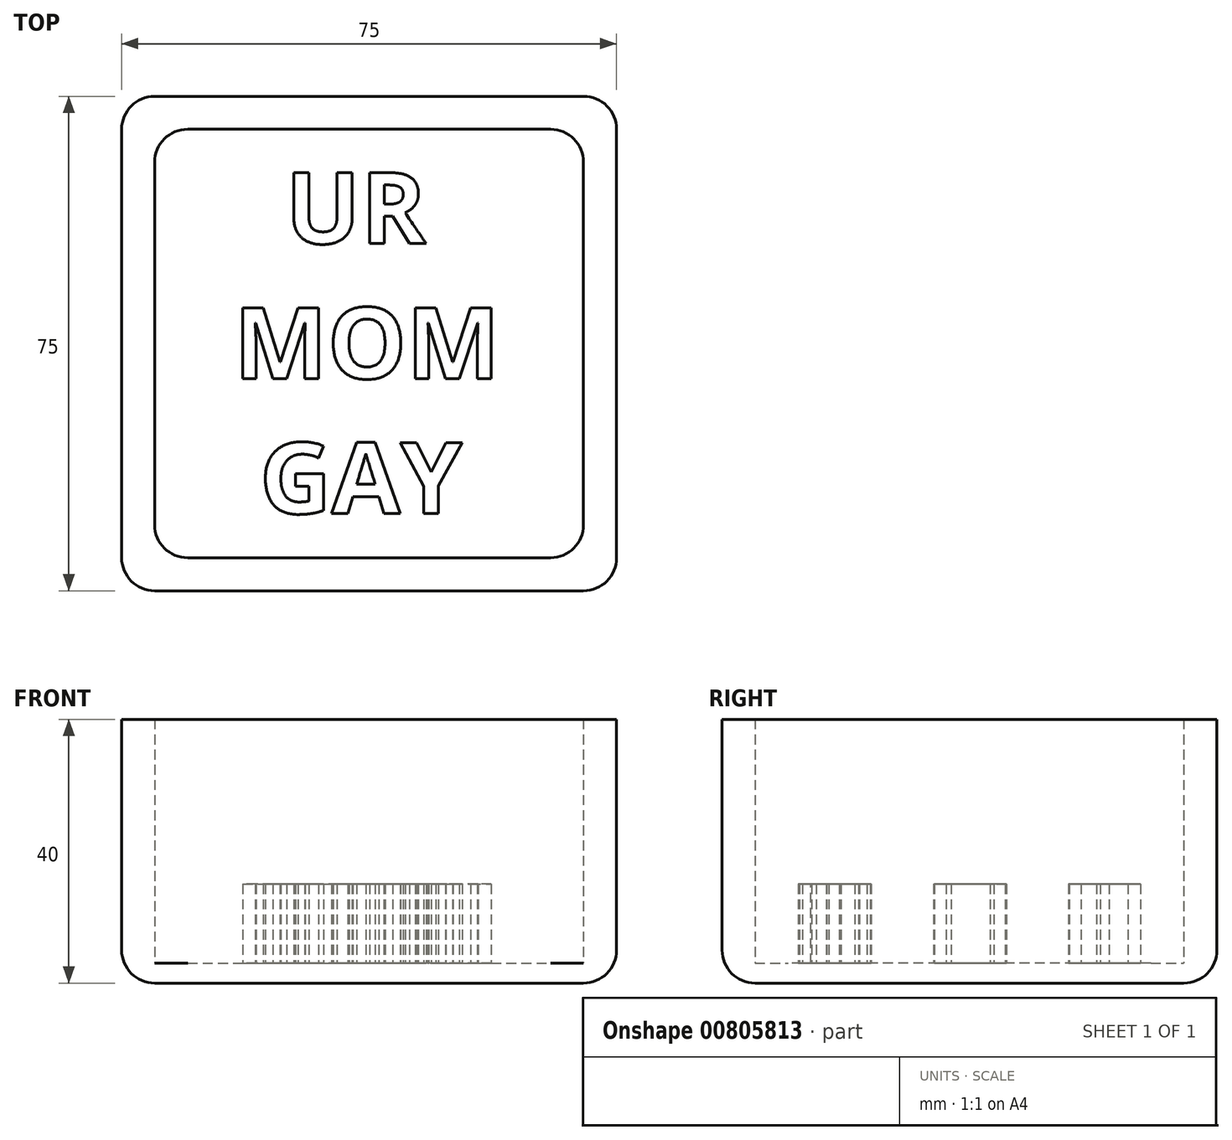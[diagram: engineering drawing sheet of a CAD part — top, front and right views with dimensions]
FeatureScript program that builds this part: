
annotation { "Feature Type Name" : "Feature", "Feature Type Description" : "" }
export const myFeature = defineFeature(function(context is Context, id is Id, definition is map)
    precondition{}
    {
        {
            var Q0;
            Q0=qCreatedBy(makeId("Top.planeOp"),FACE);
            var sketch = newSketch(context, id + "F0", { "sketchPlane" : qUnion([Q0])});
            skLineSegment(sketch, "E0.bottom", {"start": v(-33.51, 30.16) * mm, "end": v(41.49, 30.16) * mm});
            skLineSegment(sketch, "E0.top", {"start": v(-33.51, -44.84) * mm, "end": v(41.49, -44.84) * mm});
            skLineSegment(sketch, "E0.left", {"start": v(-33.51, 30.16) * mm, "end": v(-33.51, -44.84) * mm});
            skLineSegment(sketch, "E0.right", {"start": v(41.49, 30.16) * mm, "end": v(41.49, -44.84) * mm});
            skLineSegment(sketch, "E1.bottom", {"start": v(-28.51, 25.16) * mm, "end": v(36.49, 25.16) * mm});
            skLineSegment(sketch, "E1.top", {"start": v(-28.51, -39.84) * mm, "end": v(36.49, -39.84) * mm});
            skLineSegment(sketch, "E1.left", {"start": v(-28.51, 25.16) * mm, "end": v(-28.51, -39.84) * mm});
            skLineSegment(sketch, "E1.right", {"start": v(36.49, 25.16) * mm, "end": v(36.49, -39.84) * mm});
            skSolve(sketch);
        }
        {
            var Q0;
            Q0 = qSketchRegion(id + "F0", true);
            extrude(context, id + "F1", {"entities" : qUnion([Q0]), "depth" : 15 * mm, "offsetDistance" : 25 * mm});
        }
        {
            var Q0;
            Q0=makeQuery(id+"F0.imprint","IMPRINT",FACE,{"disambiguationData":[TD([[makeQuery(id+"F0.imprint","IMPRINT",EDGE,{"derivedFrom":sQuery(id+"F0.wireOp",EDGE,"E1.bottom")}),-1.0]])]});
            extrude(context, id + "F2", {"entities" : qUnion([Q0]), "operationType" : NewBodyOperationType.ADD, "depth" : 3 * mm, "offsetDistance" : 25 * mm});
        }
        {
            var Q0;
            Q0=makeQuery(id+"F1.opExtrude","SWEPT_EDGE",EDGE,{"disambiguationData":[OSD([sQuery(id+"F0.wireOp",EDGE,"E0.top"),sQuery(id+"F0.wireOp",EDGE,"E0.left")])]});
            var Q1;
            Q1=makeQuery(id+"F1.opExtrude","SWEPT_EDGE",EDGE,{"disambiguationData":[OSD([sQuery(id+"F0.wireOp",EDGE,"E0.top"),sQuery(id+"F0.wireOp",EDGE,"E0.right")])]});
            var Q2;
            Q2=makeQuery(id+"F1.opExtrude","SWEPT_EDGE",EDGE,{"disambiguationData":[OSD([sQuery(id+"F0.wireOp",EDGE,"E0.bottom"),sQuery(id+"F0.wireOp",EDGE,"E0.right")])]});
            var Q3;
            Q3=makeQuery(id+"F1.opExtrude","SWEPT_EDGE",EDGE,{"disambiguationData":[OSD([sQuery(id+"F0.wireOp",EDGE,"E0.bottom"),sQuery(id+"F0.wireOp",EDGE,"E0.left")])]});
            var Q4;
            Q4=makeQuery(id+"F1.opExtrude","CAP_EDGE",EDGE,{"disambiguationData":[OSD([sQuery(id+"F0.wireOp",EDGE,"E0.bottom")])],"isStart":true});
            var Q5;
            Q5=makeQuery(id+"F1.opExtrude","CAP_EDGE",EDGE,{"disambiguationData":[OSD([sQuery(id+"F0.wireOp",EDGE,"E0.right")])],"isStart":true});
            var Q6;
            Q6=makeQuery(id+"F1.opExtrude","CAP_EDGE",EDGE,{"disambiguationData":[OSD([sQuery(id+"F0.wireOp",EDGE,"E0.top")])],"isStart":true});
            var Q7;
            Q7=makeQuery(id+"F1.opExtrude","CAP_EDGE",EDGE,{"disambiguationData":[OSD([sQuery(id+"F0.wireOp",EDGE,"E0.left")])],"isStart":true});
            var Q8;
            Q8=makeQuery(id+"F2.opExtrude","CAP_EDGE",EDGE,{"disambiguationData":[OSD([sQuery(id+"F0.wireOp",EDGE,"E1.bottom")])],"isStart":false});
            var Q9;
            Q9=makeQuery(id+"F2.opExtrude","CAP_EDGE",EDGE,{"disambiguationData":[OSD([sQuery(id+"F0.wireOp",EDGE,"E1.right")])],"isStart":false});
            var Q10;
            Q10=makeQuery(id+"F2.opExtrude","CAP_EDGE",EDGE,{"disambiguationData":[OSD([sQuery(id+"F0.wireOp",EDGE,"E1.left")])],"isStart":false});
            var Q11;
            Q11=makeQuery(id+"F2.opExtrude","CAP_EDGE",EDGE,{"disambiguationData":[OSD([sQuery(id+"F0.wireOp",EDGE,"E1.top")])],"isStart":false});
            fillet(context, id + "F3", {"entities" : qUnion([Q0, Q1, Q2, Q3, Q4, Q5, Q6, Q7, Q8, Q9, Q10, Q11]), "radius" : 5 * mm, "tangentPropagation" : true, "allowEdgeOverflow" : false});
        }
        {
            var Q0;
            Q0=makeQuery(id+"F2.opExtrude","CAP_FACE",FACE,{"disambiguationData":[OSD([sQuery(id+"F0.wireOp",EDGE,"E1.bottom"),sQuery(id+"F0.wireOp",EDGE,"E1.top"),sQuery(id+"F0.wireOp",EDGE,"E1.left"),sQuery(id+"F0.wireOp",EDGE,"E1.right")])],"isStart":false});
            var sketch = newSketch(context, id + "F4", { "sketchPlane" : qUnion([Q0])});
            skText(sketch, "E2", { "text": "  UR\nMOM\n GAY", "fontName": "OpenSans-Bold.ttf"});
            const initialGuessF4  = {"E2": [-0.01651, 0.00782, 1, 0, 0.01084]};
            skSetInitialGuess(sketch, initialGuessF4);
            skSolve(sketch);
        }
        {
            var Q0;
            Q0 = qSketchRegion(id + "F4", true);
            extrude(context, id + "F5", {"entities" : qUnion([Q0]), "operationType" : NewBodyOperationType.ADD, "depth" : 5 * mm, "offsetDistance" : 25 * mm});
        }
        {
            var Q0;
            Q0=makeQuery(id+"F1.opExtrude","SWEPT_EDGE",EDGE,{"disambiguationData":[OSD([sQuery(id+"F0.wireOp",EDGE,"E1.bottom"),sQuery(id+"F0.wireOp",EDGE,"E1.left")])]});
            var Q1;
            Q1=makeQuery(id+"F1.opExtrude","SWEPT_EDGE",EDGE,{"disambiguationData":[OSD([sQuery(id+"F0.wireOp",EDGE,"E1.bottom"),sQuery(id+"F0.wireOp",EDGE,"E1.right")])]});
            var Q2;
            Q2=makeQuery(id+"F1.opExtrude","SWEPT_EDGE",EDGE,{"disambiguationData":[OSD([sQuery(id+"F0.wireOp",EDGE,"E1.top"),sQuery(id+"F0.wireOp",EDGE,"E1.left")])]});
            var Q3;
            Q3=makeQuery(id+"F1.opExtrude","SWEPT_EDGE",EDGE,{"disambiguationData":[OSD([sQuery(id+"F0.wireOp",EDGE,"E1.top"),sQuery(id+"F0.wireOp",EDGE,"E1.right")])]});
            fillet(context, id + "F6", {"entities" : qUnion([Q0, Q1, Q2, Q3]), "radius" : 5 * mm, "tangentPropagation" : true, "allowEdgeOverflow" : false});
        }
        {
            var Q0;
            Q0=makeQuery(id+"F5.opExtrude","CAP_FACE",FACE,{"disambiguationData":[OSD([sQuery(id+"F4.wireOp",EDGE,"E2.sketch_text.stroke-34"),sQuery(id+"F4.wireOp",EDGE,"E2.sketch_text.stroke-35"),sQuery(id+"F4.wireOp",EDGE,"E2.sketch_text.stroke-36"),sQuery(id+"F4.wireOp",EDGE,"E2.sketch_text.stroke-37"),sQuery(id+"F4.wireOp",EDGE,"E2.sketch_text.stroke-38"),sQuery(id+"F4.wireOp",EDGE,"E2.sketch_text.stroke-39"),sQuery(id+"F4.wireOp",EDGE,"E2.sketch_text.stroke-40"),sQuery(id+"F4.wireOp",EDGE,"E2.sketch_text.stroke-41"),sQuery(id+"F4.wireOp",EDGE,"E2.sketch_text.stroke-42"),sQuery(id+"F4.wireOp",EDGE,"E2.sketch_text.stroke-43"),sQuery(id+"F4.wireOp",EDGE,"E2.sketch_text.stroke-44"),sQuery(id+"F4.wireOp",EDGE,"E2.sketch_text.stroke-45"),sQuery(id+"F4.wireOp",EDGE,"E2.sketch_text.stroke-46"),sQuery(id+"F4.wireOp",EDGE,"E2.sketch_text.stroke-47"),sQuery(id+"F4.wireOp",EDGE,"E2.sketch_text.stroke-48"),sQuery(id+"F4.wireOp",EDGE,"E2.sketch_text.stroke-49"),sQuery(id+"F4.wireOp",EDGE,"E2.sketch_text.stroke-50"),sQuery(id+"F4.wireOp",EDGE,"E2.sketch_text.stroke-51"),sQuery(id+"F4.wireOp",EDGE,"E2.sketch_text.stroke-52")])],"isStart":false});
            var Q1;
            Q1=makeQuery(id+"F5.opExtrude","CAP_FACE",FACE,{"disambiguationData":[OSD([sQuery(id+"F4.wireOp",EDGE,"E2.sketch_text.stroke-53"),sQuery(id+"F4.wireOp",EDGE,"E2.sketch_text.stroke-54"),sQuery(id+"F4.wireOp",EDGE,"E2.sketch_text.stroke-55"),sQuery(id+"F4.wireOp",EDGE,"E2.sketch_text.stroke-56"),sQuery(id+"F4.wireOp",EDGE,"E2.sketch_text.stroke-57"),sQuery(id+"F4.wireOp",EDGE,"E2.sketch_text.stroke-58"),sQuery(id+"F4.wireOp",EDGE,"E2.sketch_text.stroke-59"),sQuery(id+"F4.wireOp",EDGE,"E2.sketch_text.stroke-60"),sQuery(id+"F4.wireOp",EDGE,"E2.sketch_text.stroke-61"),sQuery(id+"F4.wireOp",EDGE,"E2.sketch_text.stroke-62"),sQuery(id+"F4.wireOp",EDGE,"E2.sketch_text.stroke-63"),sQuery(id+"F4.wireOp",EDGE,"E2.sketch_text.stroke-64"),sQuery(id+"F4.wireOp",EDGE,"E2.sketch_text.stroke-65"),sQuery(id+"F4.wireOp",EDGE,"E2.sketch_text.stroke-66")])],"isStart":false});
            var Q2;
            Q2=makeQuery(id+"F5.opExtrude","CAP_FACE",FACE,{"disambiguationData":[OSD([sQuery(id+"F4.wireOp",EDGE,"E2.sketch_text.stroke-67"),sQuery(id+"F4.wireOp",EDGE,"E2.sketch_text.stroke-68"),sQuery(id+"F4.wireOp",EDGE,"E2.sketch_text.stroke-69"),sQuery(id+"F4.wireOp",EDGE,"E2.sketch_text.stroke-70"),sQuery(id+"F4.wireOp",EDGE,"E2.sketch_text.stroke-71"),sQuery(id+"F4.wireOp",EDGE,"E2.sketch_text.stroke-72"),sQuery(id+"F4.wireOp",EDGE,"E2.sketch_text.stroke-73"),sQuery(id+"F4.wireOp",EDGE,"E2.sketch_text.stroke-74"),sQuery(id+"F4.wireOp",EDGE,"E2.sketch_text.stroke-75"),sQuery(id+"F4.wireOp",EDGE,"E2.sketch_text.stroke-76"),sQuery(id+"F4.wireOp",EDGE,"E2.sketch_text.stroke-77"),sQuery(id+"F4.wireOp",EDGE,"E2.sketch_text.stroke-78"),sQuery(id+"F4.wireOp",EDGE,"E2.sketch_text.stroke-79"),sQuery(id+"F4.wireOp",EDGE,"E2.sketch_text.stroke-80"),sQuery(id+"F4.wireOp",EDGE,"E2.sketch_text.stroke-81"),sQuery(id+"F4.wireOp",EDGE,"E2.sketch_text.stroke-82"),sQuery(id+"F4.wireOp",EDGE,"E2.sketch_text.stroke-83"),sQuery(id+"F4.wireOp",EDGE,"E2.sketch_text.stroke-84"),sQuery(id+"F4.wireOp",EDGE,"E2.sketch_text.stroke-85")])],"isStart":false});
            var Q3;
            Q3=makeQuery(id+"F5.opExtrude","CAP_FACE",FACE,{"disambiguationData":[OSD([sQuery(id+"F4.wireOp",EDGE,"E2.sketch_text.stroke-15"),sQuery(id+"F4.wireOp",EDGE,"E2.sketch_text.stroke-16"),sQuery(id+"F4.wireOp",EDGE,"E2.sketch_text.stroke-17"),sQuery(id+"F4.wireOp",EDGE,"E2.sketch_text.stroke-18"),sQuery(id+"F4.wireOp",EDGE,"E2.sketch_text.stroke-19"),sQuery(id+"F4.wireOp",EDGE,"E2.sketch_text.stroke-20"),sQuery(id+"F4.wireOp",EDGE,"E2.sketch_text.stroke-21"),sQuery(id+"F4.wireOp",EDGE,"E2.sketch_text.stroke-22"),sQuery(id+"F4.wireOp",EDGE,"E2.sketch_text.stroke-23"),sQuery(id+"F4.wireOp",EDGE,"E2.sketch_text.stroke-24"),sQuery(id+"F4.wireOp",EDGE,"E2.sketch_text.stroke-25"),sQuery(id+"F4.wireOp",EDGE,"E2.sketch_text.stroke-26"),sQuery(id+"F4.wireOp",EDGE,"E2.sketch_text.stroke-27"),sQuery(id+"F4.wireOp",EDGE,"E2.sketch_text.stroke-28"),sQuery(id+"F4.wireOp",EDGE,"E2.sketch_text.stroke-29"),sQuery(id+"F4.wireOp",EDGE,"E2.sketch_text.stroke-30"),sQuery(id+"F4.wireOp",EDGE,"E2.sketch_text.stroke-31"),sQuery(id+"F4.wireOp",EDGE,"E2.sketch_text.stroke-32"),sQuery(id+"F4.wireOp",EDGE,"E2.sketch_text.stroke-33")])],"isStart":false});
            var Q4;
            Q4=makeQuery(id+"F5.opExtrude","CAP_FACE",FACE,{"disambiguationData":[OSD([sQuery(id+"F4.wireOp",EDGE,"E2.sketch_text.stroke-0"),sQuery(id+"F4.wireOp",EDGE,"E2.sketch_text.stroke-1"),sQuery(id+"F4.wireOp",EDGE,"E2.sketch_text.stroke-2"),sQuery(id+"F4.wireOp",EDGE,"E2.sketch_text.stroke-3"),sQuery(id+"F4.wireOp",EDGE,"E2.sketch_text.stroke-4"),sQuery(id+"F4.wireOp",EDGE,"E2.sketch_text.stroke-5"),sQuery(id+"F4.wireOp",EDGE,"E2.sketch_text.stroke-6"),sQuery(id+"F4.wireOp",EDGE,"E2.sketch_text.stroke-7"),sQuery(id+"F4.wireOp",EDGE,"E2.sketch_text.stroke-8"),sQuery(id+"F4.wireOp",EDGE,"E2.sketch_text.stroke-9"),sQuery(id+"F4.wireOp",EDGE,"E2.sketch_text.stroke-10"),sQuery(id+"F4.wireOp",EDGE,"E2.sketch_text.stroke-11"),sQuery(id+"F4.wireOp",EDGE,"E2.sketch_text.stroke-12"),sQuery(id+"F4.wireOp",EDGE,"E2.sketch_text.stroke-13"),sQuery(id+"F4.wireOp",EDGE,"E2.sketch_text.stroke-14")])],"isStart":false});
            var Q5;
            Q5=makeQuery(id+"F5.opExtrude","CAP_FACE",FACE,{"disambiguationData":[OSD([sQuery(id+"F4.wireOp",EDGE,"E2.sketch_text.stroke-117"),sQuery(id+"F4.wireOp",EDGE,"E2.sketch_text.stroke-118"),sQuery(id+"F4.wireOp",EDGE,"E2.sketch_text.stroke-119"),sQuery(id+"F4.wireOp",EDGE,"E2.sketch_text.stroke-120"),sQuery(id+"F4.wireOp",EDGE,"E2.sketch_text.stroke-121"),sQuery(id+"F4.wireOp",EDGE,"E2.sketch_text.stroke-122"),sQuery(id+"F4.wireOp",EDGE,"E2.sketch_text.stroke-123"),sQuery(id+"F4.wireOp",EDGE,"E2.sketch_text.stroke-124"),sQuery(id+"F4.wireOp",EDGE,"E2.sketch_text.stroke-125")])],"isStart":false});
            var Q6;
            Q6=makeQuery(id+"F5.opExtrude","CAP_FACE",FACE,{"disambiguationData":[OSD([sQuery(id+"F4.wireOp",EDGE,"E2.sketch_text.stroke-105"),sQuery(id+"F4.wireOp",EDGE,"E2.sketch_text.stroke-106"),sQuery(id+"F4.wireOp",EDGE,"E2.sketch_text.stroke-107"),sQuery(id+"F4.wireOp",EDGE,"E2.sketch_text.stroke-108"),sQuery(id+"F4.wireOp",EDGE,"E2.sketch_text.stroke-109"),sQuery(id+"F4.wireOp",EDGE,"E2.sketch_text.stroke-110"),sQuery(id+"F4.wireOp",EDGE,"E2.sketch_text.stroke-111"),sQuery(id+"F4.wireOp",EDGE,"E2.sketch_text.stroke-112"),sQuery(id+"F4.wireOp",EDGE,"E2.sketch_text.stroke-113"),sQuery(id+"F4.wireOp",EDGE,"E2.sketch_text.stroke-114"),sQuery(id+"F4.wireOp",EDGE,"E2.sketch_text.stroke-115"),sQuery(id+"F4.wireOp",EDGE,"E2.sketch_text.stroke-116")])],"isStart":false});
            var Q7;
            Q7=makeQuery(id+"F5.opExtrude","CAP_FACE",FACE,{"disambiguationData":[OSD([sQuery(id+"F4.wireOp",EDGE,"E2.sketch_text.stroke-86"),sQuery(id+"F4.wireOp",EDGE,"E2.sketch_text.stroke-87"),sQuery(id+"F4.wireOp",EDGE,"E2.sketch_text.stroke-88"),sQuery(id+"F4.wireOp",EDGE,"E2.sketch_text.stroke-89"),sQuery(id+"F4.wireOp",EDGE,"E2.sketch_text.stroke-90"),sQuery(id+"F4.wireOp",EDGE,"E2.sketch_text.stroke-91"),sQuery(id+"F4.wireOp",EDGE,"E2.sketch_text.stroke-92"),sQuery(id+"F4.wireOp",EDGE,"E2.sketch_text.stroke-93"),sQuery(id+"F4.wireOp",EDGE,"E2.sketch_text.stroke-94"),sQuery(id+"F4.wireOp",EDGE,"E2.sketch_text.stroke-95"),sQuery(id+"F4.wireOp",EDGE,"E2.sketch_text.stroke-96"),sQuery(id+"F4.wireOp",EDGE,"E2.sketch_text.stroke-97"),sQuery(id+"F4.wireOp",EDGE,"E2.sketch_text.stroke-98"),sQuery(id+"F4.wireOp",EDGE,"E2.sketch_text.stroke-99"),sQuery(id+"F4.wireOp",EDGE,"E2.sketch_text.stroke-100"),sQuery(id+"F4.wireOp",EDGE,"E2.sketch_text.stroke-101"),sQuery(id+"F4.wireOp",EDGE,"E2.sketch_text.stroke-102"),sQuery(id+"F4.wireOp",EDGE,"E2.sketch_text.stroke-103"),sQuery(id+"F4.wireOp",EDGE,"E2.sketch_text.stroke-104")])],"isStart":false});
            extrude(context, id + "F7", {"entities" : qUnion([Q0, Q1, Q2, Q3, Q4, Q5, Q6, Q7]), "operationType" : NewBodyOperationType.ADD, "depth" : 7 * mm, "offsetDistance" : 25 * mm});
        }
        {
            var Q0;
            Q0=makeQuery(id+"F1.opExtrude","CAP_FACE",FACE,{"disambiguationData":[OSD([sQuery(id+"F0.wireOp",EDGE,"E0.bottom"),sQuery(id+"F0.wireOp",EDGE,"E0.top"),sQuery(id+"F0.wireOp",EDGE,"E0.left"),sQuery(id+"F0.wireOp",EDGE,"E0.right"),sQuery(id+"F0.wireOp",EDGE,"E1.bottom"),sQuery(id+"F0.wireOp",EDGE,"E1.top"),sQuery(id+"F0.wireOp",EDGE,"E1.left"),sQuery(id+"F0.wireOp",EDGE,"E1.right")])],"isStart":false});
            extrude(context, id + "F8", {"entities" : qUnion([Q0]), "operationType" : NewBodyOperationType.ADD, "depth" : 25 * mm, "offsetDistance" : 25 * mm});
        }
    });
